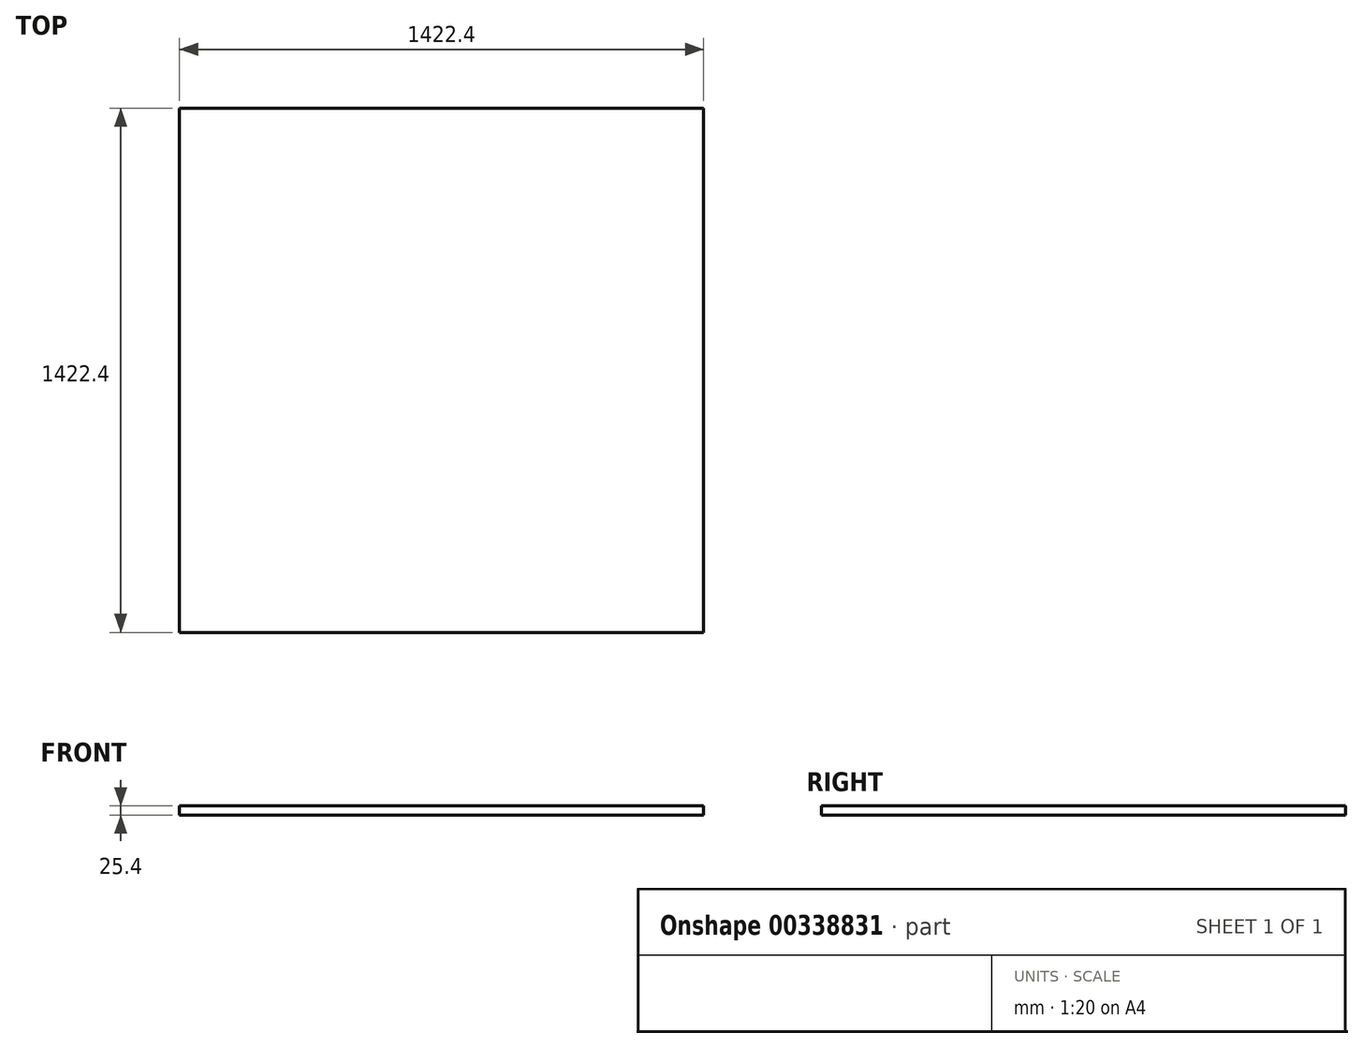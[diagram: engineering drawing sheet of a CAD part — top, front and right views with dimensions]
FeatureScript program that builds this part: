
annotation { "Feature Type Name" : "Feature", "Feature Type Description" : "" }
export const myFeature = defineFeature(function(context is Context, id is Id, definition is map)
    precondition{}
    {
        {
            var Q0;
            Q0=qCreatedBy(makeId("Top.planeOp"),FACE);
            var sketch = newSketch(context, id + "F0", { "sketchPlane" : qUnion([Q0])});
            skLineSegment(sketch, "E0.bottom", {"start": v(-701.16, 941.4) * mm, "end": v(721.24, 941.4) * mm});
            skLineSegment(sketch, "E0.top", {"start": v(-701.16, -481) * mm, "end": v(721.24, -481) * mm});
            skLineSegment(sketch, "E0.left", {"start": v(-701.16, 941.4) * mm, "end": v(-701.16, -481) * mm});
            skLineSegment(sketch, "E0.right", {"start": v(721.24, 941.4) * mm, "end": v(721.24, -481) * mm});
            skSolve(sketch);
        }
        {
            var Q0;
            Q0 = qSketchRegion(id + "F0", true);
            extrude(context, id + "F1", {"entities" : qUnion([Q0]), "depth" : 25.4 * mm});
        }
    });
